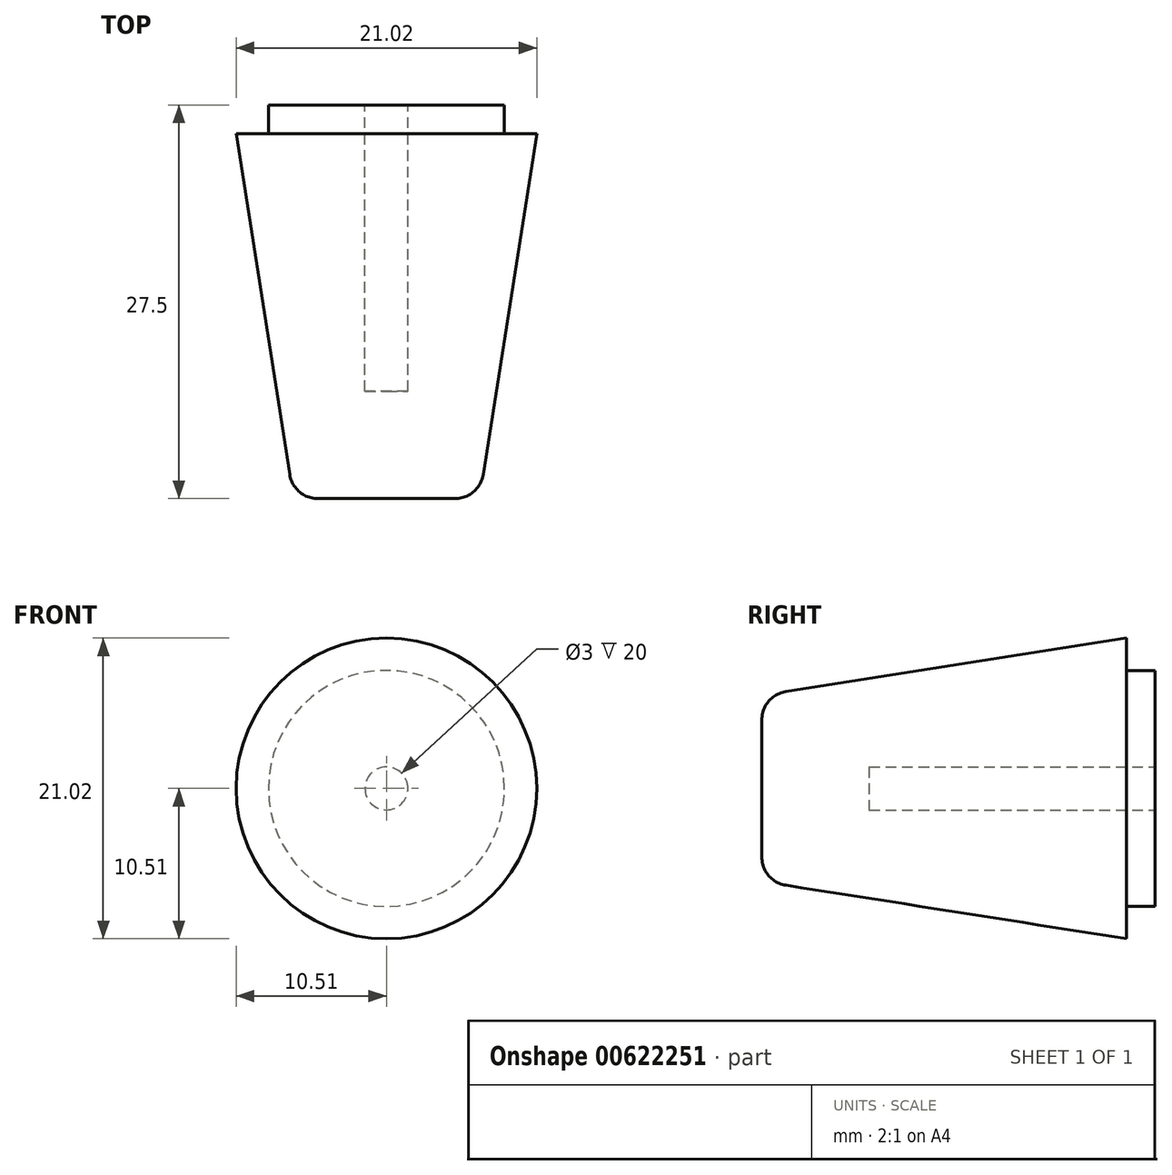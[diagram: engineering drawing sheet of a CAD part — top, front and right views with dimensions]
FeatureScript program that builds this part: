
annotation { "Feature Type Name" : "Feature", "Feature Type Description" : "" }
export const myFeature = defineFeature(function(context is Context, id is Id, definition is map)
    precondition{}
    {
        {
            var Q0;
            Q0=qCreatedBy(makeId("Front.planeOp"),FACE);
            var sketch = newSketch(context, id + "F0", { "sketchPlane" : qUnion([Q0])});
            skCircle(sketch, "E0", {"center": v(0, 0) * mm, "radius": 12 * mm});
            skSolve(sketch);
        }
        {
            var Q0;
            Q0 = qSketchRegion(id + "F0", true);
            extrude(context, id + "F1", {"entities" : qUnion([Q0]), "depth" : 25.5 * mm, "offsetDistance" : 25 * mm});
        }
        {
            var Q0;
            Q0=makeQuery(id+"F1.opExtrude","CAP_EDGE",EDGE,{"disambiguationData":[OSD([sQuery(id+"F0.wireOp",EDGE,"E0")])],"isStart":false});
            chamfer(context, id + "F2", {"entities" : qUnion([Q0]), "chamferType" : ChamferType.TWO_OFFSETS, "width1" : 5.5 * mm, "oppositeDirection" : false, "width2" : 35 * mm, "tangentPropagation" : true});
        }
        {
            var Q0;
            {var subQ0=sQuery(id+"F0.wireOp",EDGE,"E0");Q0=makeQuery(id+"F2.opChamfer","BLEND_EDGE",EDGE,{"blendedFrom":[makeQuery(id+"F1.opExtrude","CAP_EDGE",EDGE,{"disambiguationData":[OSD([subQ0])],"isStart":false}),makeQuery(id+"F1.opExtrude","CAP_FACE",FACE,{"disambiguationData":[OSD([subQ0])],"isStart":false})],"blendedInto":[makeQuery(id+"F1.opExtrude","CAP_FACE",FACE,{"disambiguationData":[OSD([subQ0])],"isStart":false})]});}
            fillet(context, id + "F3", {"entities" : qUnion([Q0]), "radius" : 2 * mm, "tangentPropagation" : true, "allowEdgeOverflow" : false});
        }
        {
            var Q0;
            Q0=makeQuery(id+"F1.opExtrude","CAP_FACE",FACE,{"disambiguationData":[OSD([sQuery(id+"F0.wireOp",EDGE,"E0")])],"isStart":true});
            var sketch = newSketch(context, id + "F4", { "sketchPlane" : qUnion([Q0])});
            skCircle(sketch, "E1", {"center": v(0, 0) * mm, "radius": 8.25 * mm});
            skSolve(sketch);
        }
        {
            var Q0;
            Q0 = qSketchRegion(id + "F4", true);
            extrude(context, id + "F5", {"entities" : qUnion([Q0]), "operationType" : NewBodyOperationType.ADD, "depth" : 2 * mm, "offsetDistance" : 25 * mm});
        }
        {
            var Q0;
            Q0=makeQuery(id+"F5.opExtrude","CAP_FACE",FACE,{"disambiguationData":[OSD([sQuery(id+"F4.wireOp",EDGE,"E1")])],"isStart":false});
            var sketch = newSketch(context, id + "F6", { "sketchPlane" : qUnion([Q0])});
            skCircle(sketch, "E2", {"center": v(0, 0) * mm, "radius": 1.5 * mm});
            skSolve(sketch);
        }
        {
            var Q0;
            Q0 = qSketchRegion(id + "F6", true);
            extrude(context, id + "F7", {"entities" : qUnion([Q0]), "operationType" : NewBodyOperationType.REMOVE, "oppositeDirection" : true, "depth" : 20 * mm, "offsetDistance" : 25 * mm});
        }
    });
